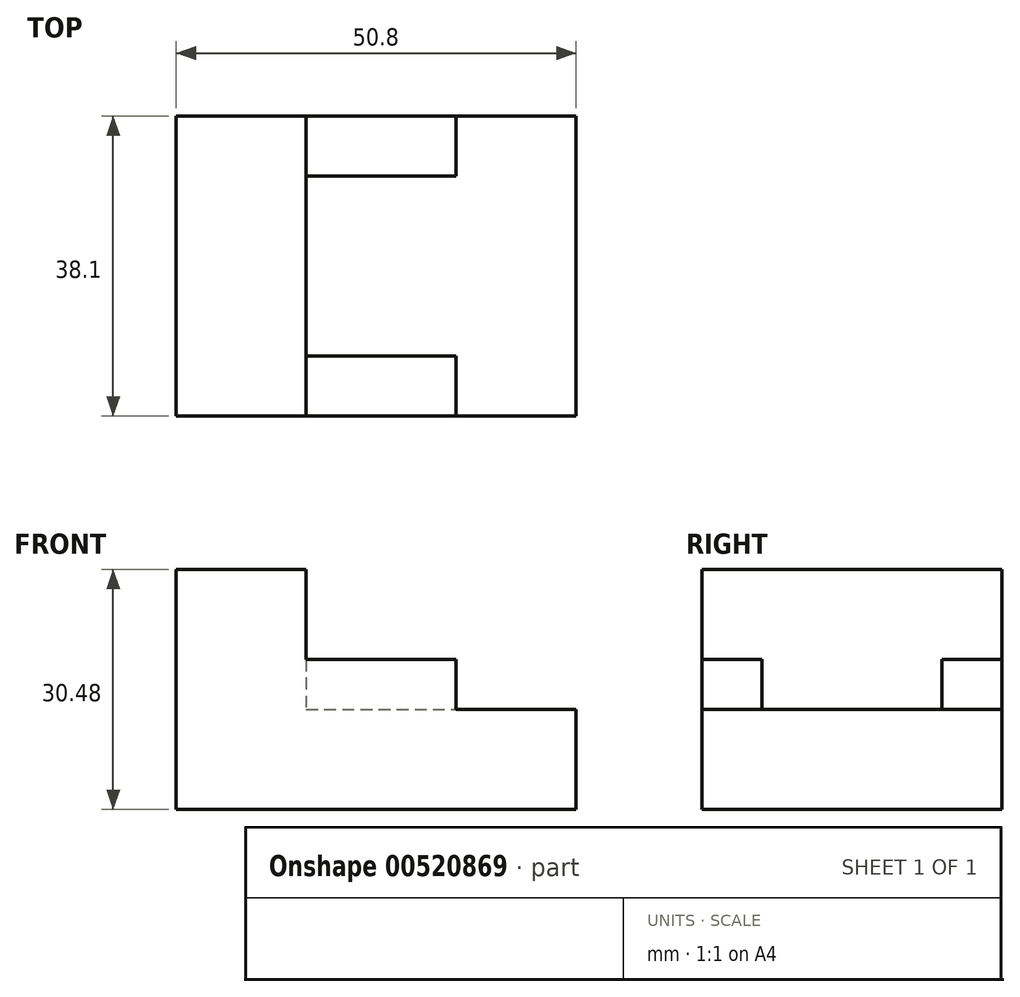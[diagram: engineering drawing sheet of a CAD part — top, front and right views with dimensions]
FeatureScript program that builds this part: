
annotation { "Feature Type Name" : "Feature", "Feature Type Description" : "" }
export const myFeature = defineFeature(function(context is Context, id is Id, definition is map)
    precondition{}
    {
        {
            var Q0;
            Q0=qCreatedBy(makeId("Top.planeOp"),FACE);
            var sketch = newSketch(context, id + "F0", { "sketchPlane" : qUnion([Q0])});
            skLineSegment(sketch, "E0.bottom", {"start": v(25.4, 19.05) * mm, "end": v(-25.4, 19.05) * mm});
            skLineSegment(sketch, "E0.top", {"start": v(25.4, -19.05) * mm, "end": v(-25.4, -19.05) * mm});
            skLineSegment(sketch, "E0.left", {"start": v(25.4, 19.05) * mm, "end": v(25.4, -19.05) * mm});
            skLineSegment(sketch, "E0.right", {"start": v(-25.4, 19.05) * mm, "end": v(-25.4, -19.05) * mm});
            skPoint(sketch, "E0.middle", {"position": v(0, 0) * mm});
            skSolve(sketch);
        }
        {
            var Q0;
            Q0=makeQuery(id+"F0.imprint","IMPRINT",FACE,{"disambiguationData":[TD([[makeQuery(id+"F0.imprint","IMPRINT",EDGE,{"derivedFrom":sQuery(id+"F0.wireOp",EDGE,"E0.bottom")}),1.0]])]});
            extrude(context, id + "F1", {"entities" : qUnion([Q0]), "depth" : 12.7 * mm, "offsetDistance" : 25.4 * mm});
        }
        {
            var Q0;
            Q0=makeQuery(id+"F1.opExtrude","CAP_FACE",FACE,{"disambiguationData":[OSD([sQuery(id+"F0.wireOp",EDGE,"E0.bottom"),sQuery(id+"F0.wireOp",EDGE,"E0.top"),sQuery(id+"F0.wireOp",EDGE,"E0.left"),sQuery(id+"F0.wireOp",EDGE,"E0.right")])],"isStart":false});
            var sketch = newSketch(context, id + "F2", { "sketchPlane" : qUnion([Q0])});
            skLineSegment(sketch, "E1.bottom", {"start": v(-8.9, -19.05) * mm, "end": v(10.16, -19.05) * mm});
            skLineSegment(sketch, "E1.top", {"start": v(-8.9, -11.43) * mm, "end": v(10.16, -11.43) * mm});
            skLineSegment(sketch, "E1.left", {"start": v(-8.9, -19.05) * mm, "end": v(-8.9, -11.43) * mm});
            skLineSegment(sketch, "E1.right", {"start": v(10.16, -19.05) * mm, "end": v(10.16, -11.43) * mm});
            skLineSegment(sketch, "E2.bottom", {"start": v(-8.9, 19.05) * mm, "end": v(10.16, 19.05) * mm});
            skLineSegment(sketch, "E2.top", {"start": v(-8.9, 11.43) * mm, "end": v(10.16, 11.43) * mm});
            skLineSegment(sketch, "E2.left", {"start": v(-8.9, 19.05) * mm, "end": v(-8.9, 11.43) * mm});
            skLineSegment(sketch, "E2.right", {"start": v(10.16, 19.05) * mm, "end": v(10.16, 11.43) * mm});
            skSolve(sketch);
        }
        {
            var Q0;
            Q0 = qSketchRegion(id + "F2", true);
            extrude(context, id + "F3", {"entities" : qUnion([Q0]), "operationType" : NewBodyOperationType.ADD, "depth" : 6.35 * mm, "offsetDistance" : 25.4 * mm});
        }
        {
            var Q0;
            Q0=makeQuery(id+"F1.opExtrude","CAP_FACE",FACE,{"disambiguationData":[OSD([sQuery(id+"F0.wireOp",EDGE,"E0.bottom"),sQuery(id+"F0.wireOp",EDGE,"E0.top"),sQuery(id+"F0.wireOp",EDGE,"E0.left"),sQuery(id+"F0.wireOp",EDGE,"E0.right")])],"isStart":false});
            var sketch = newSketch(context, id + "F4", { "sketchPlane" : qUnion([Q0])});
            skPoint(sketch, "E3.firstSnap0", {"position": v(-8.9, -15.87) * mm});
            skLineSegment(sketch, "E3.bottom", {"start": v(-25.4, -19.05) * mm, "end": v(-8.9, -19.05) * mm});
            skLineSegment(sketch, "E3.top", {"start": v(-25.4, 19.05) * mm, "end": v(-8.9, 19.05) * mm});
            skLineSegment(sketch, "E3.left", {"start": v(-25.4, -19.05) * mm, "end": v(-25.4, 19.05) * mm});
            skLineSegment(sketch, "E3.right", {"start": v(-8.9, -15.87) * mm, "end": v(-8.9, 19.05) * mm});
            skSolve(sketch);
        }
        {
            var Q0;
            Q0 = qSketchRegion(id + "F4", true);
            extrude(context, id + "F5", {"entities" : qUnion([Q0]), "operationType" : NewBodyOperationType.ADD, "depth" : 17.78 * mm, "offsetDistance" : 25.4 * mm});
        }
    });
